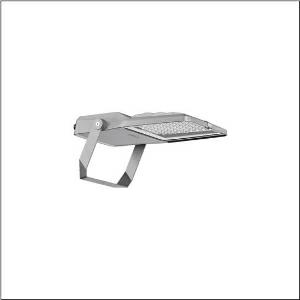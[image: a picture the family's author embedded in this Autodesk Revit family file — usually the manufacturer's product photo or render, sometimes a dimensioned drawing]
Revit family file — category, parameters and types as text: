
# Revit family: floodlight_fl_21_iq_mini___rs12_5xa7771d2b1a_498a
name_source: partatom
category: Lighting Fixtures
units: mm (PartAtom-declared; Revit-internal decimal feet)

## family parameters
Cut with Voids When Loaded = No
Host = Face
Light Source = No
Part Type = Normal
Room Calculation Point = No
Round Connector Dimension = Use Diameter
Shared = No

## types (1)
- --- (1 x LED, 18020 lm, 143 W, 3000K)
    Apparent Load = 143 VA
    CIE Flux Codes = 79 92 99 100 100
    Color Rendering = 70
    Color Temperature = 3000K
    Default Elevation = 1800 mm
    Description = Floodlight FL 21 iQ mini, floodlight, primary light control with lens, of PMMA, primary optical cover: protective disc, of toughened safety glass, transparent, light distribution: RS12, light emission: direct distribution, installation type: surface-mounted, lamps: LED, High Power LED, rated values: 18.020lm | 143W | 126lm/W (begin service life); end service life: 18.020lm | 151,6W; at 50% lumin. flux: 9.010lm | 60,6W | 148,7lm/W, colour temperature: 3000K, colour rendering: CRI > 70, light colour: 730, light setting 1 begin service life: 100% | 18.020lm | 143W | 126lm/W | 3.000K, light setting 1 end service life: 151,6W, further light settings possible, control: Auto-Match, Temp-Guard, Lumen-Switch, Night-Set, Smart-Wire, Light-Fading, Desk-Remote (wireless, voltage-free reading and setting of iQ features in the workshop via application-optimized NFC function/RFID function), optimised constant luminous flux control (CLO 2.0), pre-setting: linear dimming characteristic, with terminal, 6-pole, mains connection: 220..240V, AC, 50/60Hz, luminaire housing, of diecast aluminium, powder-coated, SITECO metallic grey (DB 702S), corrosivity category C5 mid according to DIN EN ISO 12944suitable for swimming poolschlorine-resistant, sealing non-destructively replaceable, mounting bracket, of steel, galvanised, powder-coated, SITECO metallic grey (DB 702S), protection rating (complete): IP66, insulation class (complete): insulation class II (safety insulation), certification: CE, ENEC, VDE, protection symbol: D, impact resistance: IK08, permissible operating ambient temperature: -40..+40°C, permissible operating ambient temperature for outdoor applications: -40..+50°C, standard: DIN EN 12944, LABS conformity tested according to VDMA 24364:2018-05, packaging unit: 1 piece

Light Distribution: RS12
    Height = 70 mm
    Lamp = 1 x LED
    Lamp Light Flux = 18020 lm
    Lamp Power = 143 W
    Lamp count = 1
    Length = 485 mm
    Luminous efficacy = 126 lm/W
    Manufacturer = Siteco
    ModVariant = No
    Model = 5XA7771D2B1A
    Number of Poles = 1
    OnlyDefault = Yes
    Power Factor = 1
    Product Name = Floodlight FL 21 iQ mini | RS12
    Product group = floodlight | pylon annexe
    ProductGroupID = 6201
    Protection Class = Protection class II
    Protection Degree = IP 66
    RLX_Detail_Level = 1
    RLX_Emergency_Light_Flux = 0 lm
    RLX_Emergency_Type = 0
    RLX_Emergency_Type_DB = No
    RlxData = <blob elided: 91417 chars, md5=c20fe262>
    Socket = socket
    Standby Power = 0 W
    System Light Flux = 18020 lm
    System Power = 143 W
    Type Comments = factory setting: luminous flux: 100 % | dim-lin: 254 | 730 mA
    Type Image = l_1006845.jpg
    URL = http://relux.com
    VarID = @adj_166967
    Voltage = 0 V
    Weight = 0.00 kg
    Width = 337 mm

## geometry (parser evidence)
native form markers: Blend x4, Sweep x11
no freeform markers — native parametric forms only
